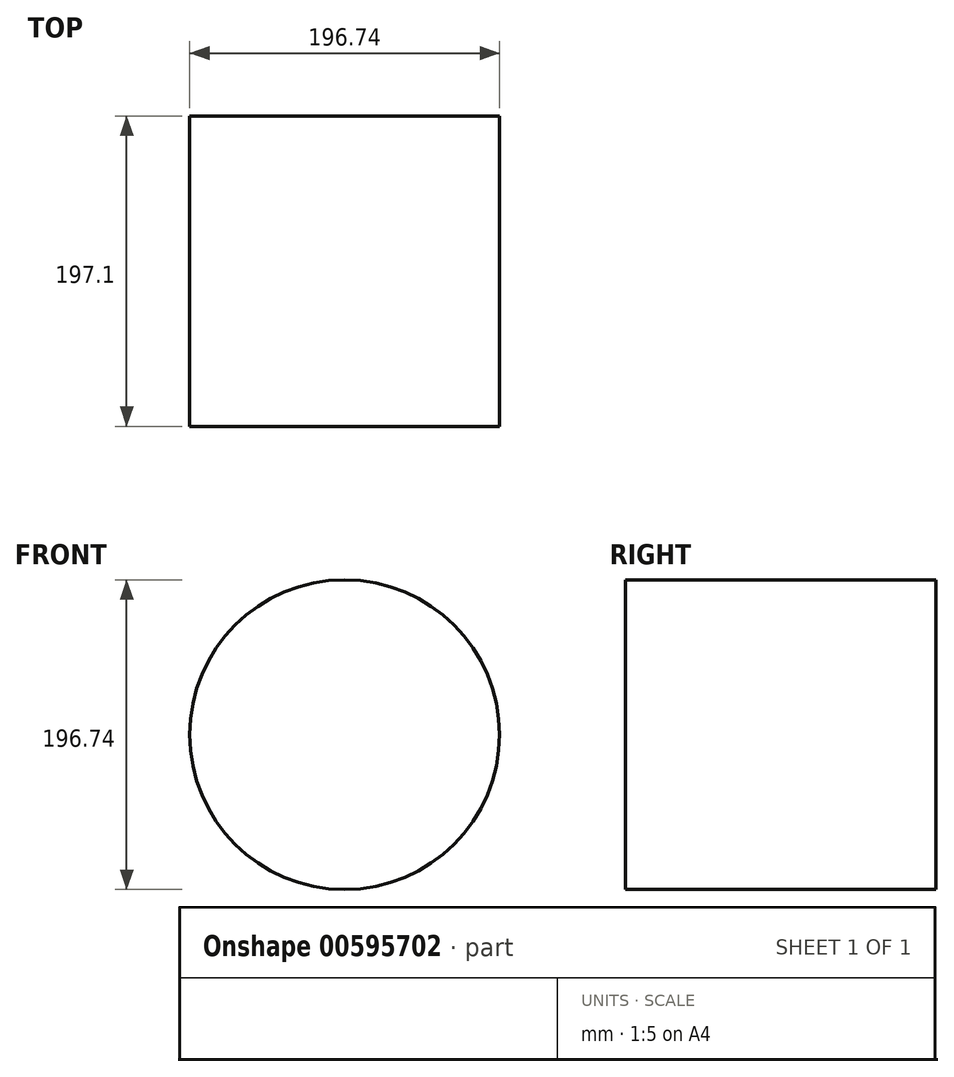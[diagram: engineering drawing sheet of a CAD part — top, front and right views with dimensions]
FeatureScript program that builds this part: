
annotation { "Feature Type Name" : "Feature", "Feature Type Description" : "" }
export const myFeature = defineFeature(function(context is Context, id is Id, definition is map)
    precondition{}
    {
        {
            var Q0;
            Q0=qCreatedBy(makeId("Front.planeOp"),FACE);
            var sketch = newSketch(context, id + "F0", { "sketchPlane" : qUnion([Q0])});
            skCircle(sketch, "E0", {"center": v(0, 0) * mm, "radius": 98.37 * mm});
            skSolve(sketch);
        }
        {
            var Q0;
            Q0=makeQuery(id+"F0.imprint","IMPRINT",FACE,{"disambiguationData":[TD([[makeQuery(id+"F0.imprint","IMPRINT",EDGE,{"derivedFrom":sQuery(id+"F0.wireOp",EDGE,"E0")}),1.0]])]});
            extrude(context, id + "F1", {"entities" : qUnion([Q0]), "depth" : 197.1 * mm, "offsetDistance" : 25.4 * mm});
        }
    });
